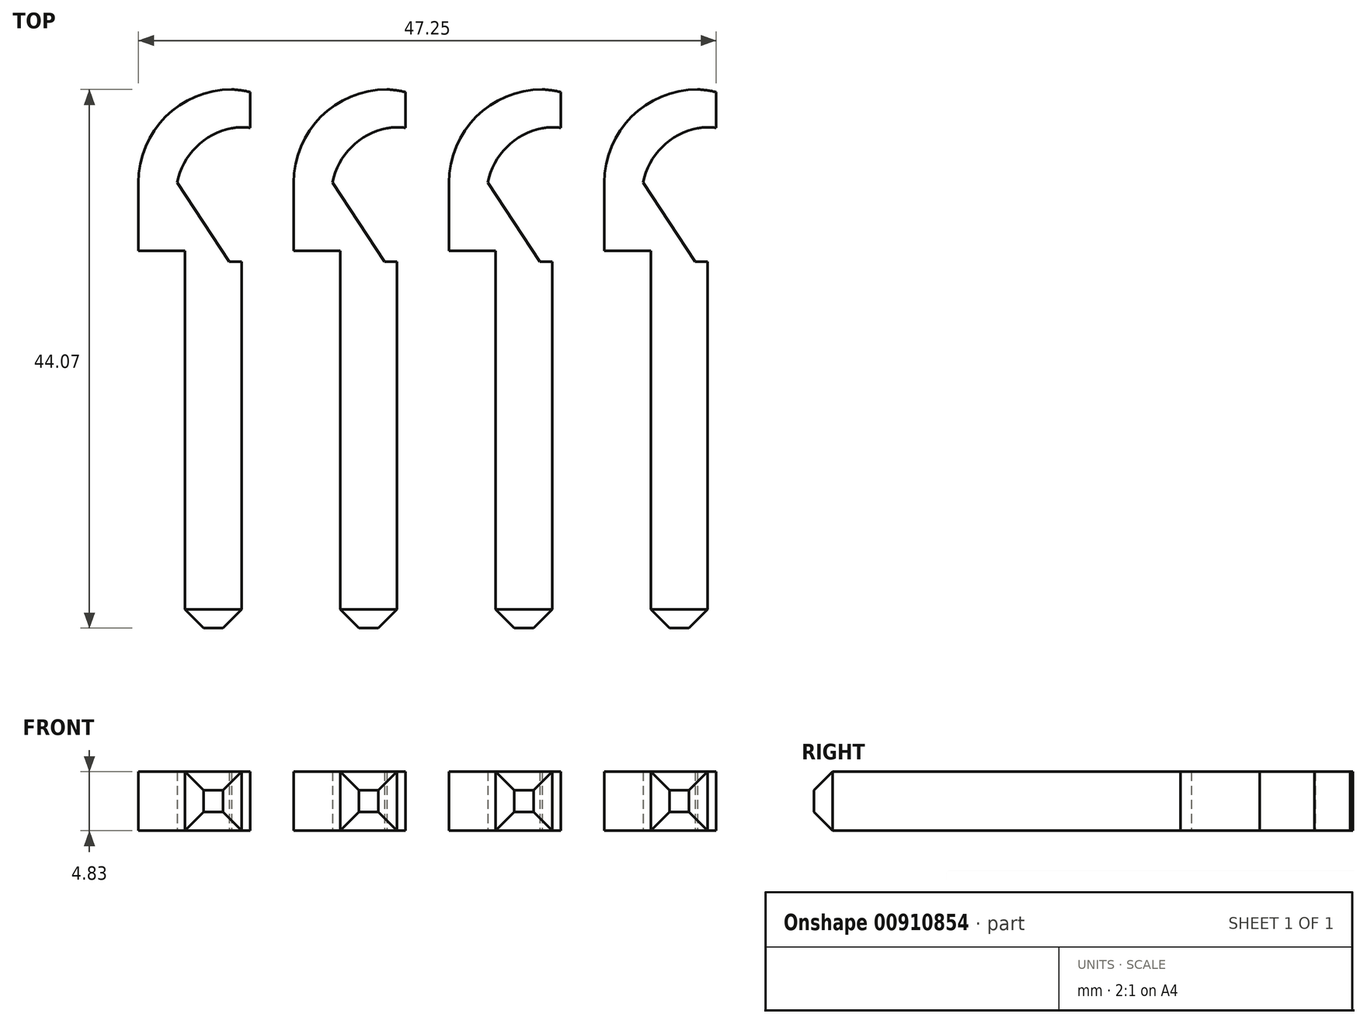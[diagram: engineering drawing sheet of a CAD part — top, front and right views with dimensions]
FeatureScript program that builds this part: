
annotation { "Feature Type Name" : "Feature", "Feature Type Description" : "" }
export const myFeature = defineFeature(function(context is Context, id is Id, definition is map)
    precondition{}
    {
        {
            var Q0;
            Q0=qCreatedBy(makeId("Top.planeOp"),FACE);
            var sketch = newSketch(context, id + "F0", { "sketchPlane" : qUnion([Q0])});
            skLineSegment(sketch, "E0.bottom", {"start": v(3.15, 0) * mm, "end": v(7.77, 0) * mm});
            skLineSegment(sketch, "E0.left", {"start": v(-0.66, 30.86) * mm, "end": v(-0.66, 36.45) * mm});
            skArc(sketch, "E1", {"start": v(6.96, 44.07) * mm, "mid": v(1.57, 41.84) * mm, "end": v(-0.66, 36.45) * mm});
            skArc(sketch, "E2", {"start": v(6.96, 40.9) * mm, "mid": v(4.05, 39.35) * mm, "end": v(2.51, 36.45) * mm});
            skLineSegment(sketch, "E3", {"start": v(7.77, 29.97) * mm, "end": v(6.76, 29.97) * mm});
            skLineSegment(sketch, "E4", {"start": v(2.51, 36.45) * mm, "end": v(6.76, 29.97) * mm});
            skLineSegment(sketch, "E5", {"start": v(-0.66, 30.86) * mm, "end": v(3.15, 30.86) * mm});
            skLineSegment(sketch, "E6", {"start": v(3.15, 30.86) * mm, "end": v(3.15, 0) * mm});
            skArc(sketch, "E7", {"start": v(8.5, 40.92) * mm, "mid": v(7.72, 40.97) * mm, "end": v(6.96, 40.9) * mm});
            skArc(sketch, "E8", {"start": v(8.5, 43.85) * mm, "mid": v(7.73, 44) * mm, "end": v(6.96, 44.07) * mm});
            skLineSegment(sketch, "E9", {"start": v(8.5, 43.85) * mm, "end": v(8.5, 40.92) * mm});
            skLineSegment(sketch, "E10", {"start": v(7.77, 29.97) * mm, "end": v(7.77, 0) * mm});
            skSolve(sketch);
        }
        {
            var Q0;
            Q0=makeQuery(id+"F0.imprint","IMPRINT",FACE,{"disambiguationData":[TD([[makeQuery(id+"F0.imprint","IMPRINT",EDGE,{"derivedFrom":sQuery(id+"F0.wireOp",EDGE,"E0.bottom")}),1.0]])]});
            extrude(context, id + "F1", {"entities" : qUnion([Q0]), "depth" : 4.83 * mm, "offsetDistance" : 25.4 * mm});
        }
        {
            var Q0;
            Q0=makeQuery(id+"F1.opExtrude","CAP_EDGE",EDGE,{"disambiguationData":[OSD([sQuery(id+"F0.wireOp",EDGE,"E0.bottom"),sQuery(id+"F0.wireOp",EDGE,"PLzhcY2A-30Kq-YQ2q-5JEC-efN0CIueV3yo")])],"isStart":true});
            var Q1;
            Q1=makeQuery(id+"F1.opExtrude","SWEPT_EDGE",EDGE,{"disambiguationData":[OSD([sQuery(id+"F0.wireOp",EDGE,"E0.bottom"),sQuery(id+"F0.wireOp",EDGE,"E6")])]});
            var Q2;
            Q2=makeQuery(id+"F1.opExtrude","SWEPT_EDGE",EDGE,{"disambiguationData":[OSD([sQuery(id+"F0.wireOp",EDGE,"i1VOEegX-Xz9x-DhTO-umMd-qcNygYNa7A8m"),sQuery(id+"F0.wireOp",EDGE,"PLzhcY2A-30Kq-YQ2q-5JEC-efN0CIueV3yo")])]});
            var Q3;
            Q3=makeQuery(id+"F1.opExtrude","CAP_EDGE",EDGE,{"disambiguationData":[OSD([sQuery(id+"F0.wireOp",EDGE,"E0.bottom"),sQuery(id+"F0.wireOp",EDGE,"PLzhcY2A-30Kq-YQ2q-5JEC-efN0CIueV3yo")])],"isStart":false});
            chamfer(context, id + "F2", {"entities" : qUnion([Q0, Q1, Q2, Q3]), "width" : 1.52 * mm, "tangentPropagation" : true});
        }
        {
            var Q0;
            Q0=makeQuery(id+"F1.opExtrude","SWEPT_EDGE",EDGE,{"disambiguationData":[OSD([sQuery(id+"F0.wireOp",EDGE,"E0.bottom"),sQuery(id+"F0.wireOp",EDGE,"E10")])]});
            chamfer(context, id + "F3", {"entities" : qUnion([Q0]), "width" : 1.52 * mm, "tangentPropagation" : true});
        }
        {
            var Q0;
            Q0=makeQuery(id+"F1.opExtrude","SWEPT_BODY",BODY,{"disambiguationData":[OSD([sQuery(id+"F0.wireOp",EDGE,"E0.bottom"),sQuery(id+"F0.wireOp",EDGE,"E0.left"),sQuery(id+"F0.wireOp",EDGE,"E1"),sQuery(id+"F0.wireOp",EDGE,"E2"),sQuery(id+"F0.wireOp",EDGE,"E3"),sQuery(id+"F0.wireOp",EDGE,"E4"),sQuery(id+"F0.wireOp",EDGE,"E5"),sQuery(id+"F0.wireOp",EDGE,"E6"),sQuery(id+"F0.wireOp",EDGE,"E7"),sQuery(id+"F0.wireOp",EDGE,"E8"),sQuery(id+"F0.wireOp",EDGE,"E9"),sQuery(id+"F0.wireOp",EDGE,"E10")])]});
            transform(context, id + "F4", {"entities" : qUnion([Q0]), "transformType" : TransformType.TRANSLATION_3D, "dx" : 12.7 * mm, "dy" : 0 * mm, "dz" : 0 * mm, "makeCopy" : true});
        }
        {
            var Q0;
            Q0=makeQuery(id+"F4.opPattern","COPY",BODY,{"derivedFrom":makeQuery(id+"F1.opExtrude","SWEPT_BODY",BODY,{"disambiguationData":[OSD([sQuery(id+"F0.wireOp",EDGE,"E0.bottom"),sQuery(id+"F0.wireOp",EDGE,"E0.left"),sQuery(id+"F0.wireOp",EDGE,"E1"),sQuery(id+"F0.wireOp",EDGE,"E2"),sQuery(id+"F0.wireOp",EDGE,"E3"),sQuery(id+"F0.wireOp",EDGE,"E4"),sQuery(id+"F0.wireOp",EDGE,"E5"),sQuery(id+"F0.wireOp",EDGE,"E6"),sQuery(id+"F0.wireOp",EDGE,"E7"),sQuery(id+"F0.wireOp",EDGE,"E8"),sQuery(id+"F0.wireOp",EDGE,"E9"),sQuery(id+"F0.wireOp",EDGE,"E10")])]}),"instanceName":"1"});
            transform(context, id + "F5", {"entities" : qUnion([Q0]), "transformType" : TransformType.TRANSLATION_3D, "dx" : 12.7 * mm, "dy" : 0 * mm, "dz" : 0 * mm, "makeCopy" : true});
        }
        {
            var Q0;
            Q0=makeQuery(id+"F5.opPattern","COPY",BODY,{"derivedFrom":makeQuery(id+"F4.opPattern","COPY",BODY,{"derivedFrom":makeQuery(id+"F1.opExtrude","SWEPT_BODY",BODY,{"disambiguationData":[OSD([sQuery(id+"F0.wireOp",EDGE,"E0.bottom"),sQuery(id+"F0.wireOp",EDGE,"E0.left"),sQuery(id+"F0.wireOp",EDGE,"E1"),sQuery(id+"F0.wireOp",EDGE,"E2"),sQuery(id+"F0.wireOp",EDGE,"E3"),sQuery(id+"F0.wireOp",EDGE,"E4"),sQuery(id+"F0.wireOp",EDGE,"E5"),sQuery(id+"F0.wireOp",EDGE,"E6"),sQuery(id+"F0.wireOp",EDGE,"E7"),sQuery(id+"F0.wireOp",EDGE,"E8"),sQuery(id+"F0.wireOp",EDGE,"E9"),sQuery(id+"F0.wireOp",EDGE,"E10")])]}),"instanceName":"1"}),"instanceName":"1"});
            transform(context, id + "F6", {"entities" : qUnion([Q0]), "transformType" : TransformType.TRANSLATION_3D, "dx" : 12.7 * mm, "dy" : 0 * mm, "dz" : 0 * mm, "makeCopy" : true});
        }
    });
